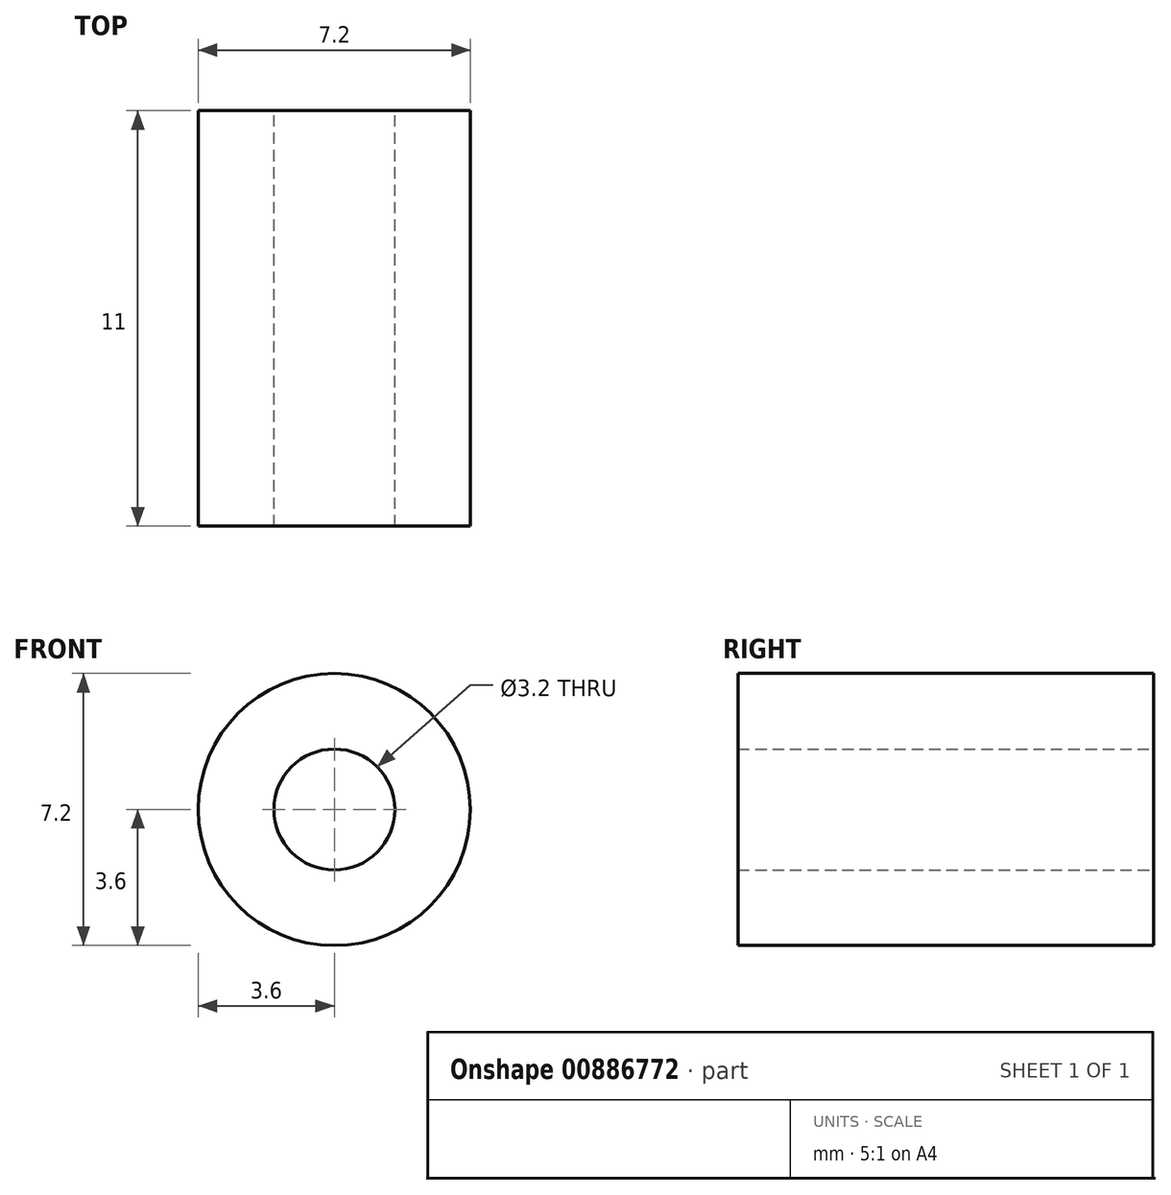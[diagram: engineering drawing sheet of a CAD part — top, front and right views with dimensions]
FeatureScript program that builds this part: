
annotation { "Feature Type Name" : "Feature", "Feature Type Description" : "" }
export const myFeature = defineFeature(function(context is Context, id is Id, definition is map)
    precondition{}
    {
        {
            var Q0;
            Q0=qCreatedBy(makeId("Front.planeOp"),FACE);
            var sketch = newSketch(context, id + "F0", { "sketchPlane" : qUnion([Q0])});
            skCircle(sketch, "E0", {"center": v(0, 0) * mm, "radius": 1.6 * mm});
            skCircle(sketch, "E1.0", {"center": v(0, 0) * mm, "radius": 3.6 * mm});
            skSolve(sketch);
        }
        {
            var Q0;
            Q0 = qSketchRegion(id + "F0", true);
            extrude(context, id + "F1", {"entities" : qUnion([Q0]), "depth" : 11 * mm, "offsetDistance" : 25 * mm});
        }
    });
